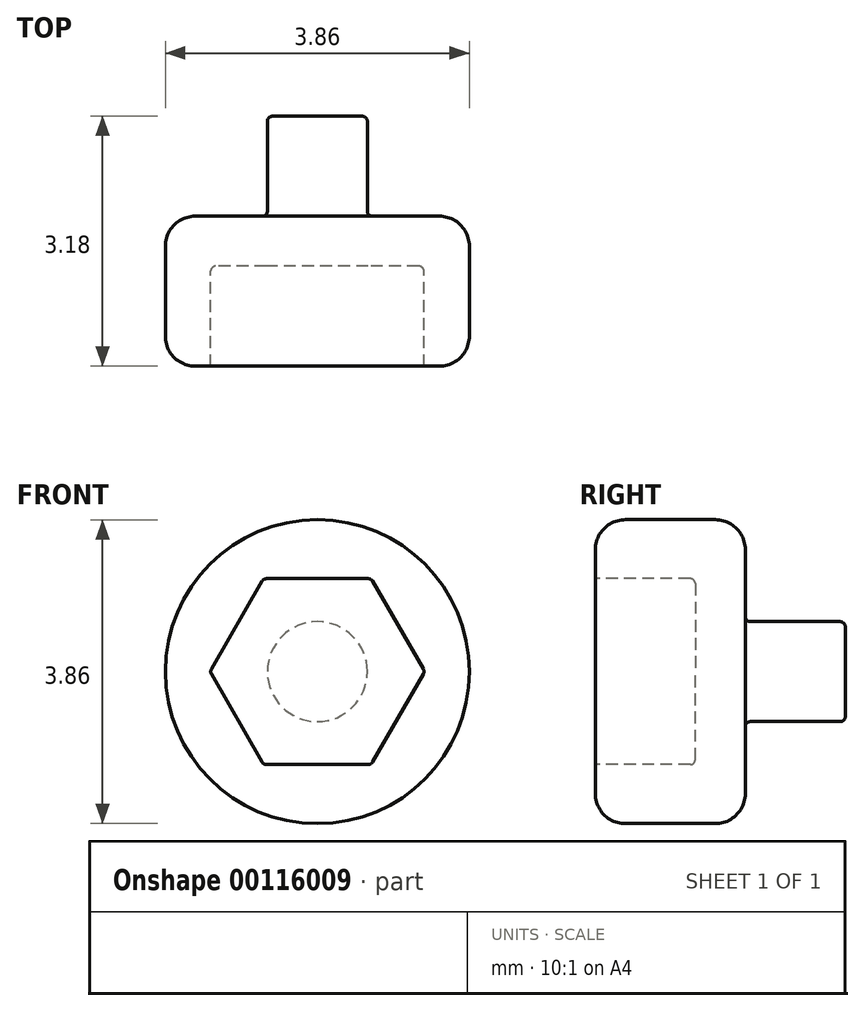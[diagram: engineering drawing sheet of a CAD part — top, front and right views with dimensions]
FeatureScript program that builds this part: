
annotation { "Feature Type Name" : "Feature", "Feature Type Description" : "" }
export const myFeature = defineFeature(function(context is Context, id is Id, definition is map)
    precondition{}
    {
        {
            var Q0;
            Q0=qCreatedBy(makeId("Top.planeOp"),FACE);
            var sketch = newSketch(context, id + "F0", { "sketchPlane" : qUnion([Q0])});
            skLineSegment(sketch, "E0", {"start": v(0, -1.83) * mm, "end": v(0, 1.35) * mm});
            skLineSegment(sketch, "E1", {"start": v(0, 1.35) * mm, "end": v(-0.63, 1.35) * mm});
            skLineSegment(sketch, "E2", {"start": v(-0.64, 1.35) * mm, "end": v(-0.63, 0.08) * mm});
            skLineSegment(sketch, "E3", {"start": v(-0.63, 0.08) * mm, "end": v(-1.93, 0.08) * mm});
            skLineSegment(sketch, "E4", {"start": v(-1.93, 0.08) * mm, "end": v(-1.93, -1.83) * mm});
            skLineSegment(sketch, "E5", {"start": v(-1.93, -1.83) * mm, "end": v(0, -1.83) * mm});
            skSolve(sketch);
        }
        {
            var Q0;
            Q0 = qSketchRegion(id + "F0", true);
            var Q1;
            Q1=sQuery(id+"F0.wireOp",EDGE,"E0");
            revolve(context, id + "F1", {"entities" : qUnion([Q0]), "axis" : qUnion([Q1]), "revolveType" : RevolveType.FULL});
        }
        {
            var Q0;
            Q0=makeQuery(id+"F1.opRevolve","SWEPT_FACE",FACE,{"disambiguationData":[OSD([sQuery(id+"F0.wireOp",EDGE,"E5")])]});
            var sketch = newSketch(context, id + "F2", { "sketchPlane" : qUnion([Q0])});
            skCircle(sketch, "E6.cCircle", {"center": v(0, 0) * mm, "radius": 1.18 * mm, "construction": true});
            skLineSegment(sketch, "E6.0", {"start": v(-0.68, 1.18) * mm, "end": v(0.68, 1.18) * mm});
            skLineSegment(sketch, "E6.1", {"start": v(0.68, 1.18) * mm, "end": v(1.36, 0) * mm});
            skLineSegment(sketch, "E6.2", {"start": v(1.36, 0) * mm, "end": v(0.68, -1.18) * mm});
            skLineSegment(sketch, "E6.3", {"start": v(0.68, -1.18) * mm, "end": v(-0.68, -1.18) * mm});
            skLineSegment(sketch, "E6.4", {"start": v(-0.68, -1.18) * mm, "end": v(-1.36, 0) * mm});
            skLineSegment(sketch, "E6.5", {"start": v(-1.36, 0) * mm, "end": v(-0.68, 1.18) * mm});
            skPoint(sketch, "E6.0.midPoint", {"position": v(0, 1.18) * mm});
            skSolve(sketch);
        }
        {
            var Q0;
            Q0 = qSketchRegion(id + "F2", true);
            extrude(context, id + "F3", {"entities" : qUnion([Q0]), "operationType" : NewBodyOperationType.REMOVE, "oppositeDirection" : true, "depth" : 1.27 * mm});
        }
        {
            var Q0;
            Q0=makeQuery(id+"F1.opRevolve","SWEPT_EDGE",EDGE,{"disambiguationData":[OSD([sQuery(id+"F0.wireOp",EDGE,"E4"),sQuery(id+"F0.wireOp",EDGE,"E5")])]});
            var Q1;
            Q1=makeQuery(id+"F1.opRevolve","SWEPT_EDGE",EDGE,{"disambiguationData":[OSD([sQuery(id+"F0.wireOp",EDGE,"E3"),sQuery(id+"F0.wireOp",EDGE,"E4")])]});
            fillet(context, id + "F4", {"entities" : qUnion([Q0, Q1]), "radius" : 0.38 * mm, "tangentPropagation" : true, "allowEdgeOverflow" : false});
        }
        {
            var Q0;
            Q0=makeQuery(id+"F3.boolean.opBoolean","COPY",EDGE,{"derivedFrom":makeQuery(id+"F3.opExtrude","CAP_EDGE",EDGE,{"disambiguationData":[OSD([sQuery(id+"F2.wireOp",EDGE,"E6.0")])],"isStart":true})});
            var Q1;
            Q1=makeQuery(id+"F3.boolean.opBoolean","COPY",EDGE,{"derivedFrom":makeQuery(id+"F3.opExtrude","CAP_EDGE",EDGE,{"disambiguationData":[OSD([sQuery(id+"F2.wireOp",EDGE,"E6.1")])],"isStart":true})});
            var Q2;
            Q2=makeQuery(id+"F3.boolean.opBoolean","COPY",EDGE,{"derivedFrom":makeQuery(id+"F3.opExtrude","CAP_EDGE",EDGE,{"disambiguationData":[OSD([sQuery(id+"F2.wireOp",EDGE,"E6.2")])],"isStart":true})});
            var Q3;
            Q3=makeQuery(id+"F3.boolean.opBoolean","COPY",EDGE,{"derivedFrom":makeQuery(id+"F3.opExtrude","CAP_EDGE",EDGE,{"disambiguationData":[OSD([sQuery(id+"F2.wireOp",EDGE,"E6.4")])],"isStart":true})});
            var Q4;
            Q4=makeQuery(id+"F3.boolean.opBoolean","COPY",EDGE,{"derivedFrom":makeQuery(id+"F3.opExtrude","CAP_EDGE",EDGE,{"disambiguationData":[OSD([sQuery(id+"F2.wireOp",EDGE,"E6.5")])],"isStart":true})});
            var Q5;
            Q5=makeQuery(id+"F3.boolean.opBoolean","COPY",EDGE,{"derivedFrom":makeQuery(id+"F3.opExtrude","CAP_EDGE",EDGE,{"disambiguationData":[OSD([sQuery(id+"F2.wireOp",EDGE,"E6.1")])],"isStart":false})});
            var Q6;
            Q6=makeQuery(id+"F3.boolean.opBoolean","COPY",EDGE,{"derivedFrom":makeQuery(id+"F3.opExtrude","CAP_EDGE",EDGE,{"disambiguationData":[OSD([sQuery(id+"F2.wireOp",EDGE,"E6.2")])],"isStart":false})});
            var Q7;
            Q7=makeQuery(id+"F3.boolean.opBoolean","COPY",EDGE,{"derivedFrom":makeQuery(id+"F3.opExtrude","CAP_EDGE",EDGE,{"disambiguationData":[OSD([sQuery(id+"F2.wireOp",EDGE,"E6.0")])],"isStart":false})});
            var Q8;
            Q8=makeQuery(id+"F3.boolean.opBoolean","COPY",EDGE,{"derivedFrom":makeQuery(id+"F3.opExtrude","CAP_EDGE",EDGE,{"disambiguationData":[OSD([sQuery(id+"F2.wireOp",EDGE,"E6.5")])],"isStart":false})});
            var Q9;
            Q9=makeQuery(id+"F3.boolean.opBoolean","COPY",EDGE,{"derivedFrom":makeQuery(id+"F3.opExtrude","CAP_EDGE",EDGE,{"disambiguationData":[OSD([sQuery(id+"F2.wireOp",EDGE,"E6.4")])],"isStart":false})});
            var Q10;
            Q10=makeQuery(id+"F3.boolean.opBoolean","COPY",EDGE,{"derivedFrom":makeQuery(id+"F3.opExtrude","CAP_EDGE",EDGE,{"disambiguationData":[OSD([sQuery(id+"F2.wireOp",EDGE,"E6.3")])],"isStart":false})});
            var Q11;
            Q11=makeQuery(id+"F3.boolean.opBoolean","COPY",EDGE,{"derivedFrom":makeQuery(id+"F3.opExtrude","CAP_EDGE",EDGE,{"disambiguationData":[OSD([sQuery(id+"F2.wireOp",EDGE,"E6.3")])],"isStart":true})});
            var Q12;
            Q12=makeQuery(id+"F3.boolean.opBoolean","COPY",EDGE,{"derivedFrom":makeQuery(id+"F3.opExtrude","SWEPT_EDGE",EDGE,{"disambiguationData":[OSD([sQuery(id+"F2.wireOp",EDGE,"E6.0"),sQuery(id+"F2.wireOp",EDGE,"E6.1")])]})});
            var Q13;
            Q13=makeQuery(id+"F3.boolean.opBoolean","COPY",EDGE,{"derivedFrom":makeQuery(id+"F3.opExtrude","SWEPT_EDGE",EDGE,{"disambiguationData":[OSD([sQuery(id+"F2.wireOp",EDGE,"E6.0"),sQuery(id+"F2.wireOp",EDGE,"E6.5")])]})});
            var Q14;
            Q14=makeQuery(id+"F3.boolean.opBoolean","COPY",EDGE,{"derivedFrom":makeQuery(id+"F3.opExtrude","SWEPT_EDGE",EDGE,{"disambiguationData":[OSD([sQuery(id+"F2.wireOp",EDGE,"E6.4"),sQuery(id+"F2.wireOp",EDGE,"E6.5")])]})});
            var Q15;
            Q15=makeQuery(id+"F3.boolean.opBoolean","COPY",EDGE,{"derivedFrom":makeQuery(id+"F3.opExtrude","SWEPT_EDGE",EDGE,{"disambiguationData":[OSD([sQuery(id+"F2.wireOp",EDGE,"E6.3"),sQuery(id+"F2.wireOp",EDGE,"E6.4")])]})});
            var Q16;
            Q16=makeQuery(id+"F3.boolean.opBoolean","COPY",EDGE,{"derivedFrom":makeQuery(id+"F3.opExtrude","SWEPT_EDGE",EDGE,{"disambiguationData":[OSD([sQuery(id+"F2.wireOp",EDGE,"E6.2"),sQuery(id+"F2.wireOp",EDGE,"E6.3")])]})});
            var Q17;
            Q17=makeQuery(id+"F3.boolean.opBoolean","COPY",EDGE,{"derivedFrom":makeQuery(id+"F3.opExtrude","SWEPT_EDGE",EDGE,{"disambiguationData":[OSD([sQuery(id+"F2.wireOp",EDGE,"E6.1"),sQuery(id+"F2.wireOp",EDGE,"E6.2")])]})});
            var Q18;
            Q18=makeQuery(id+"F1.opRevolve","SWEPT_EDGE",EDGE,{"disambiguationData":[OSD([sQuery(id+"F0.wireOp",EDGE,"E2"),sQuery(id+"F0.wireOp",EDGE,"E3")])]});
            var Q19;
            Q19=makeQuery(id+"F1.opRevolve","SWEPT_EDGE",EDGE,{"disambiguationData":[OSD([sQuery(id+"F0.wireOp",EDGE,"E1"),sQuery(id+"F0.wireOp",EDGE,"E2")])]});
            fillet(context, id + "F5", {"entities" : qUnion([Q0, Q1, Q2, Q3, Q4, Q5, Q6, Q7, Q8, Q9, Q10, Q11, Q12, Q13, Q14, Q15, Q16, Q17, Q18, Q19]), "radius" : 0.06 * mm, "tangentPropagation" : true, "allowEdgeOverflow" : false});
        }
    });
